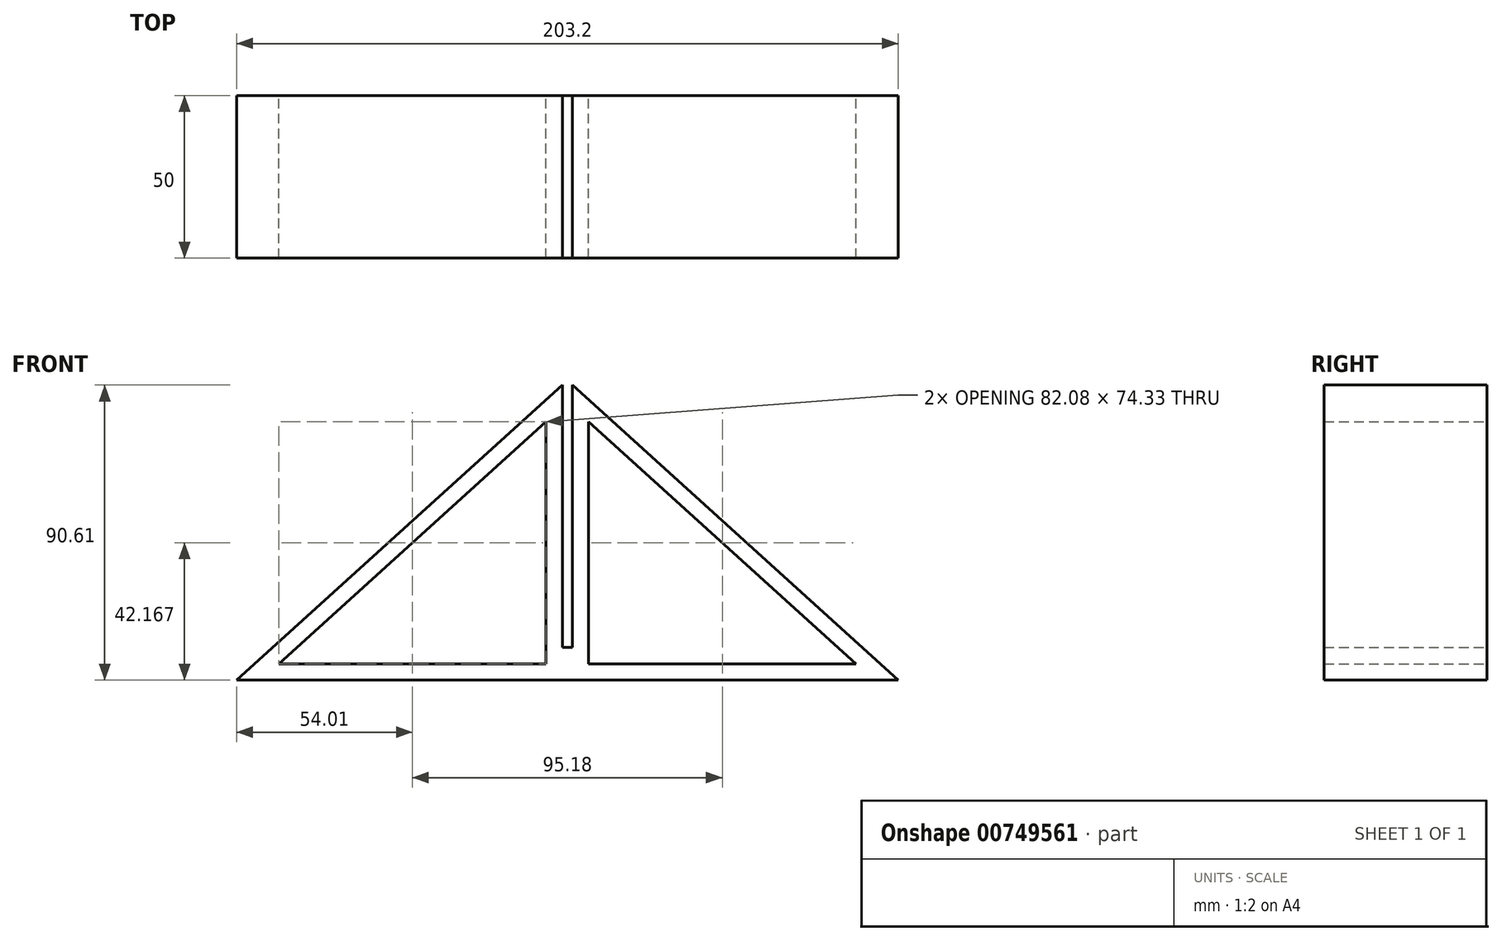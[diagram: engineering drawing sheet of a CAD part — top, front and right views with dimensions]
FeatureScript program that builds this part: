
annotation { "Feature Type Name" : "Feature", "Feature Type Description" : "" }
export const myFeature = defineFeature(function(context is Context, id is Id, definition is map)
    precondition{}
    {
        {
            var Q0;
            Q0=qCreatedBy(makeId("Front.planeOp"),FACE);
            var sketch = newSketch(context, id + "F0", { "sketchPlane" : qUnion([Q0])});
            skLineSegment(sketch, "E0", {"start": v(0, 0) * mm, "end": v(101.6, 0) * mm});
            skLineSegment(sketch, "E1", {"start": v(101.6, 0) * mm, "end": v(1.55, 90.6) * mm});
            skLineSegment(sketch, "E2", {"start": v(1.55, 90.6) * mm, "end": v(1.55, 10) * mm});
            skLineSegment(sketch, "E3", {"start": v(1.55, 10) * mm, "end": v(-1.55, 10) * mm});
            skLineSegment(sketch, "E4", {"start": v(-1.55, 10) * mm, "end": v(-1.55, 90.6) * mm});
            skLineSegment(sketch, "E5", {"start": v(-1.55, 90.6) * mm, "end": v(-101.6, 0) * mm});
            skLineSegment(sketch, "E6", {"start": v(-101.6, 0) * mm, "end": v(0, 0) * mm});
            skLineSegment(sketch, "E7.0", {"start": v(0, 5) * mm, "end": v(88.63, 5) * mm});
            skLineSegment(sketch, "E7.1", {"start": v(-88.63, 5) * mm, "end": v(0, 5) * mm});
            skLineSegment(sketch, "E7.2", {"start": v(6.55, 79.33) * mm, "end": v(6.55, 5) * mm});
            skLineSegment(sketch, "E7.3", {"start": v(6.55, 5) * mm, "end": v(-6.55, 5) * mm});
            skLineSegment(sketch, "E7.4", {"start": v(-6.55, 5) * mm, "end": v(-6.55, 79.33) * mm});
            skLineSegment(sketch, "E7.5", {"start": v(88.63, 5) * mm, "end": v(6.55, 79.33) * mm});
            skLineSegment(sketch, "E7.6", {"start": v(-6.55, 79.33) * mm, "end": v(-88.63, 5) * mm});
            skSolve(sketch);
        }
        {
            var Q0;
            Q0 = qSketchRegion(id + "F0", true);
            extrude(context, id + "F1", {"entities" : qUnion([Q0]), "endBound" : BoundingType.SYMMETRIC, "depth" : 50 * mm, "offsetDistance" : 25 * mm});
        }
    });
